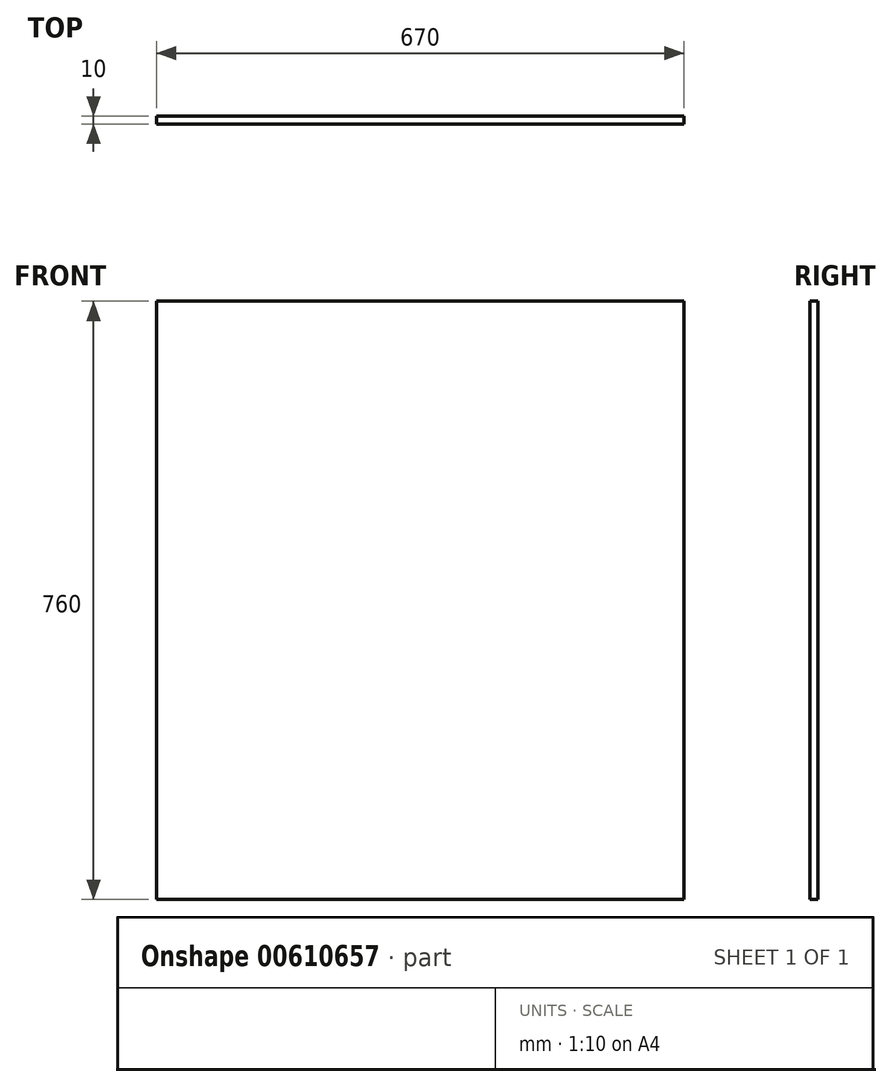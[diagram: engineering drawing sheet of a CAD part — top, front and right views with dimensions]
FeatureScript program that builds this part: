
annotation { "Feature Type Name" : "Feature", "Feature Type Description" : "" }
export const myFeature = defineFeature(function(context is Context, id is Id, definition is map)
    precondition{}
    {
        {
            var Q0;
            Q0=qCreatedBy(makeId("Front.planeOp"),FACE);
            var sketch = newSketch(context, id + "F0", { "sketchPlane" : qUnion([Q0])});
            skLineSegment(sketch, "E0.bottom", {"start": v(-279.26, 530.08) * mm, "end": v(390.74, 530.08) * mm});
            skLineSegment(sketch, "E0.top", {"start": v(-279.26, -229.92) * mm, "end": v(390.74, -229.92) * mm});
            skLineSegment(sketch, "E0.left", {"start": v(-279.26, 530.08) * mm, "end": v(-279.26, -229.92) * mm});
            skLineSegment(sketch, "E0.right", {"start": v(390.74, 530.08) * mm, "end": v(390.74, -229.92) * mm});
            skPoint(sketch, "E1.endSnap0", {"position": v(55.74, 530.08) * mm});
            skSolve(sketch);
        }
        {
            var Q0;
            Q0=makeQuery(id+"F0.imprint","IMPRINT",FACE,{"disambiguationData":[TD([[makeQuery(id+"F0.imprint","IMPRINT",EDGE,{"derivedFrom":sQuery(id+"F0.wireOp",EDGE,"E0.bottom")}),-1.0]])]});
            extrude(context, id + "F1", {"entities" : qUnion([Q0]), "depth" : 10 * mm, "offsetDistance" : 25 * mm});
        }
    });
